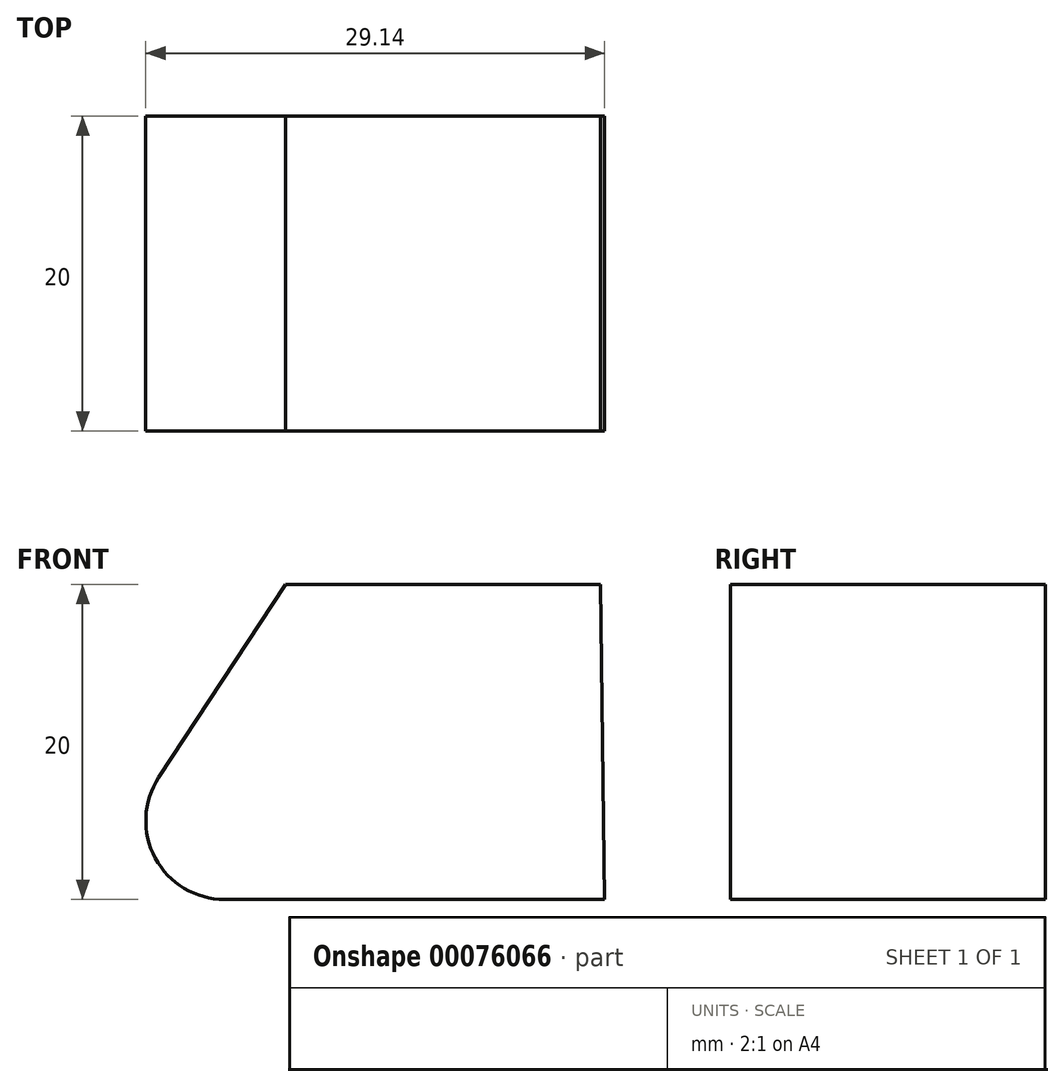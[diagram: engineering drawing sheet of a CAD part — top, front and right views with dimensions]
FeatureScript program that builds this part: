
annotation { "Feature Type Name" : "Feature", "Feature Type Description" : "" }
export const myFeature = defineFeature(function(context is Context, id is Id, definition is map)
    precondition{}
    {
        {
            var Q0;
            Q0=qCreatedBy(makeId("Front.planeOp"),FACE);
            var sketch = newSketch(context, id + "F0", { "sketchPlane" : qUnion([Q0])});
            skLineSegment(sketch, "E0", {"start": v(9.27, 0) * mm, "end": v(33.41, 0) * mm});
            skLineSegment(sketch, "E1", {"start": v(33.41, 0) * mm, "end": v(33.16, 20) * mm});
            skLineSegment(sketch, "E2", {"start": v(33.16, 20) * mm, "end": v(13.16, 20) * mm});
            skLineSegment(sketch, "E3", {"start": v(13.16, 20) * mm, "end": v(5.1, 7.75) * mm});
            skPoint(sketch, "E4.visualSharp", {"position": v(0, 0) * mm});
            skArc(sketch, "E4.filletArc", {"start": v(5.1, 7.75) * mm, "mid": v(4.87, 2.63) * mm, "end": v(9.27, 0) * mm});
            skSolve(sketch);
        }
        {
            var Q0;
            Q0 = qSketchRegion(id + "F0", true);
            extrude(context, id + "F1", {"entities" : qUnion([Q0]), "depth" : 20 * mm});
        }
    });
